# Revit family: Skrzynka rozprężna SR
name_source: partatom
category: Terminale wentylacyjne
revit_build: Autodesk Revit 2018 (Build: 20190510_1515(x64)
units: mm (PartAtom-declared; Revit-internal decimal feet)

## family parameters
Numer OmniClass = 23.75.70.21.27.11
Oparty na płaszczyźnie roboczej = Nie
Punkt obliczania pomieszczeń = Nie
Tnij formami wycięć po wczytaniu = Nie
Typ części = Normalny
Tytuł OmniClass = Diffusers, Registers, and Grilles
Współdzielony = Nie
Wymiar okrągłego złącza = Użyj średnicy
Zawsze pionowo = Tak

## types (9) — shared parameters
Atest Higieniczny = HK/K/0522/03/2016
Deklaracja zgodności = 14/DZ/2020/K
IfcExportAs = IfcFlowTerminal
Karta katalogowa = https://www.sawpol.pl
Komentarze do typu = Skrzynka rozprężna SR
Materiał = SAW-POL Stal ocynkowana
Model = SR
Obraz typu = Skrzynka.PNG
Producent = PPHU SAW-POL
URL = https://www.sawpol.pl

## per-type parameters (varying)
| type | Wielkość skrzynki | Wymiar skrzynki | Wysokość skrzynki | Średnica króćca dolotowego | Średnica króćca przyłączeniowego |
| 250 | 250 mm  [stored 0.82021 ft] | 400 mm  [stored 1.31234 ft] | 280 mm  [stored 0.918635 ft] | 198 mm  [stored 0.649606 ft] | 250 mm  [stored 0.82021 ft] |
| 315 | 315 mm  [stored 1.03346 ft] | 580 mm  [stored 1.90289 ft] | 330 mm  [stored 1.08268 ft] | 248 mm  [stored 0.813648 ft] | 315 mm  [stored 1.03346 ft] |
| 355 | 355 mm | 580 mm  [stored 1.90289 ft] | 330 mm  [stored 1.08268 ft] | 248 mm  [stored 0.813648 ft] | 355 mm |
| 400 | 400 mm  [stored 1.31234 ft] | 590 mm  [stored 1.9357 ft] | 380 mm | 313 mm  [stored 1.0269 ft] | 400 mm  [stored 1.31234 ft] |
| 500 | 500 mm  [stored 1.64042 ft] | 700 mm  [stored 2.29659 ft] | 380 mm | 313 mm  [stored 1.0269 ft] | 500 mm  [stored 1.64042 ft] |
| 630 | 630 mm  [stored 2.06693 ft] | 800 mm  [stored 2.62467 ft] | 595 mm  [stored 1.9521 ft] | 398 mm  [stored 1.30577 ft] | 630 mm  [stored 2.06693 ft] |
| 710 | 710 mm | 900 mm  [stored 2.95276 ft] | 595 mm  [stored 1.9521 ft] | 398 mm  [stored 1.30577 ft] | 710 mm |
| 800 | 800 mm  [stored 2.62467 ft] | 1000 mm  [stored 3.28084 ft] | 595 mm  [stored 1.9521 ft] | 398 mm  [stored 1.30577 ft] | 800 mm  [stored 2.62467 ft] |
| 1000 | 1000 mm  [stored 3.28084 ft] | 1250 mm  [stored 4.10105 ft] | 595 mm  [stored 1.9521 ft] | 398 mm  [stored 1.30577 ft] | 1000 mm  [stored 3.28084 ft] |

note: [stored X ft] marks values corroborated as IEEE doubles in the binary element streams (Revit-internal decimal feet)
